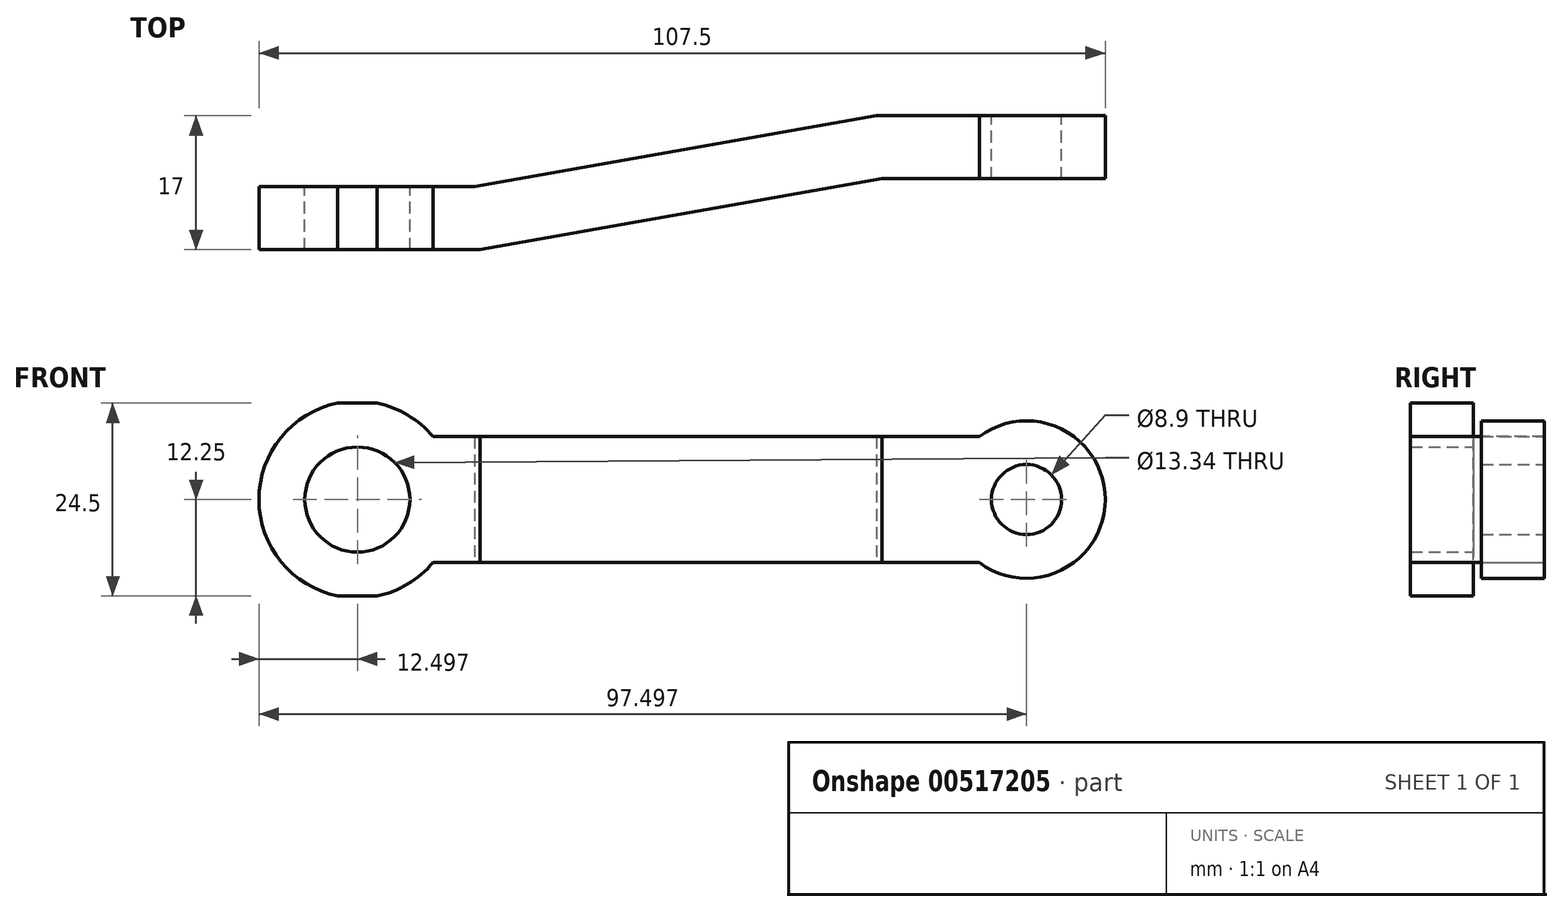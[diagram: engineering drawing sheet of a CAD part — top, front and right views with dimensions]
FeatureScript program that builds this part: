
annotation { "Feature Type Name" : "Feature", "Feature Type Description" : "" }
export const myFeature = defineFeature(function(context is Context, id is Id, definition is map)
    precondition{}
    {
        {
            var Q0;
            Q0=qCreatedBy(makeId("Front.planeOp"),FACE);
            var sketch = newSketch(context, id + "F0", { "sketchPlane" : qUnion([Q0])});
            skArc(sketch, "E0", {"start": v(-16.34, 8) * mm, "mid": v(-38.44, 0) * mm, "end": v(-16.34, -8) * mm});
            skArc(sketch, "E1", {"start": v(53.06, -8) * mm, "mid": v(69.06, 0) * mm, "end": v(53.06, 8) * mm});
            skLineSegment(sketch, "E2", {"start": v(-16.34, 8) * mm, "end": v(53.06, 8) * mm});
            skLineSegment(sketch, "E3", {"start": v(53.06, 8) * mm, "end": v(-16.34, 8) * mm});
            skLineSegment(sketch, "E4.MirrorCS", {"start": v(53.06, -8) * mm, "end": v(-16.34, -8) * mm});
            skCircle(sketch, "E5", {"center": v(-25.94, 0) * mm, "radius": 6.67 * mm});
            skCircle(sketch, "E6", {"center": v(59.06, 0) * mm, "radius": 4.45 * mm});
            skSolve(sketch);
        }
        {
            var Q0;
            Q0=makeQuery(id+"F0.imprint","IMPRINT",FACE,{"disambiguationData":[TD([[makeQuery(id+"F0.imprint","IMPRINT",EDGE,{"derivedFrom":sQuery(id+"F0.wireOp",EDGE,"E0")}),1.0]])]});
            extrude(context, id + "F1", {"entities" : qUnion([Q0]), "depth" : 25 * mm, "offsetDistance" : 25 * mm});
        }
        {
            var Q0;
            Q0=qCreatedBy(makeId("Top.planeOp"),FACE);
            var sketch = newSketch(context, id + "F2", { "sketchPlane" : qUnion([Q0])});
            skLineSegment(sketch, "E7", {"start": v(-38.44, -9) * mm, "end": v(-11.04, -9) * mm});
            skLineSegment(sketch, "E8", {"start": v(-11.04, -9) * mm, "end": v(40, 0) * mm});
            skLineSegment(sketch, "E9", {"start": v(40, 0) * mm, "end": v(69.06, 0) * mm});
            skLineSegment(sketch, "E10.0", {"start": v(40.7, -8) * mm, "end": v(69.06, -8) * mm});
            skLineSegment(sketch, "E10.1", {"start": v(-10.34, -17) * mm, "end": v(40.7, -8) * mm});
            skLineSegment(sketch, "E10.2", {"start": v(-38.44, -17) * mm, "end": v(-10.34, -17) * mm});
            skLineSegment(sketch, "E11", {"start": v(-38.44, -25) * mm, "end": v(-38.44, 0) * mm});
            skLineSegment(sketch, "E12", {"start": v(69.06, 0) * mm, "end": v(69.06, -25) * mm});
            skSolve(sketch);
        }
        {
            var Q0;
            Q0 = qSketchRegion(id + "F2", true);
            extrude(context, id + "F3", {"entities" : qUnion([Q0]), "operationType" : NewBodyOperationType.INTERSECT, "endBound" : BoundingType.SYMMETRIC, "depth" : 24.5 * mm, "offsetDistance" : 25 * mm});
        }
    });
